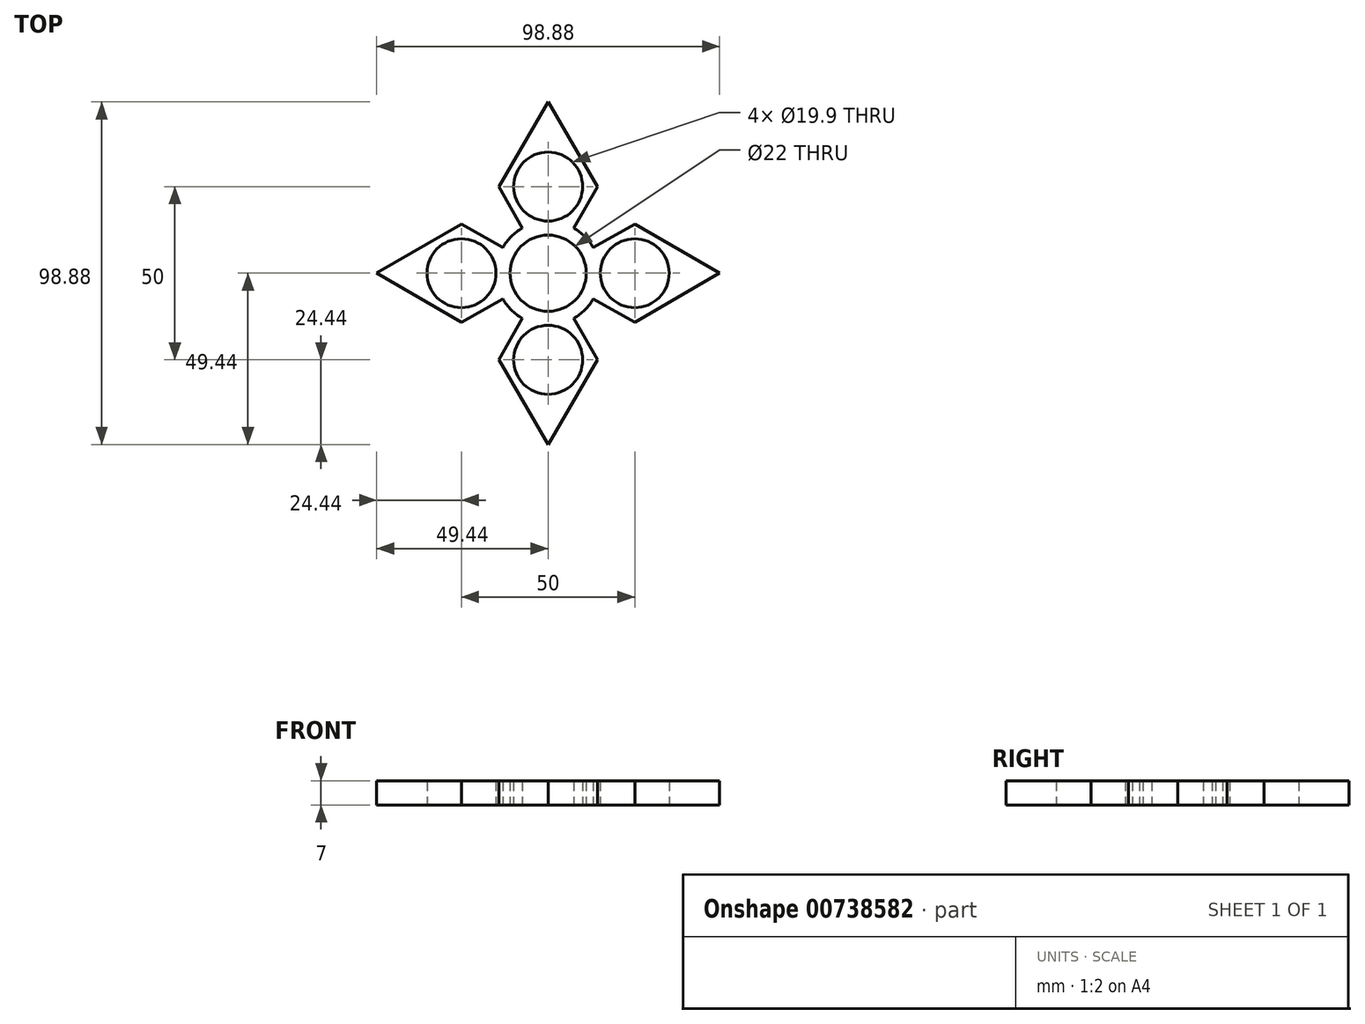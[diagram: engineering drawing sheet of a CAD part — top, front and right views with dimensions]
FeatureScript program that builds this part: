
annotation { "Feature Type Name" : "Feature", "Feature Type Description" : "" }
export const myFeature = defineFeature(function(context is Context, id is Id, definition is map)
    precondition{}
    {
        {
            var Q0;
            Q0=qCreatedBy(makeId("Top.planeOp"),FACE);
            var sketch = newSketch(context, id + "F0", { "sketchPlane" : qUnion([Q0])});
            skCircle(sketch, "E0", {"center": v(0, 0) * mm, "radius": 11 * mm});
            skArc(sketch, "E1", {"start": v(-7.41, 13.04) * mm, "mid": v(-10.6, 10.6) * mm, "end": v(-13.04, 7.41) * mm});
            skCircle(sketch, "E2", {"center": v(0, 25) * mm, "radius": 9.95 * mm});
            skLineSegment(sketch, "E3", {"start": v(0, 49.44) * mm, "end": v(14.2, 25) * mm});
            skLineSegment(sketch, "E4", {"start": v(14.2, 25) * mm, "end": v(7.41, 13.04) * mm});
            skLineSegment(sketch, "E5.MirrorCS", {"start": v(0, 49.44) * mm, "end": v(-14.2, 25) * mm});
            skLineSegment(sketch, "E6.MirrorCS", {"start": v(-14.2, 25) * mm, "end": v(-7.41, 13.04) * mm});
            skLineSegment(sketch, "E7.MirrorCS", {"start": v(14.2, -25) * mm, "end": v(7.41, -13.04) * mm});
            skLineSegment(sketch, "E8.MirrorCS", {"start": v(-14.2, -25) * mm, "end": v(-7.41, -13.04) * mm});
            skCircle(sketch, "E9.MirrorC", {"center": v(0, -25) * mm, "radius": 9.95 * mm});
            skLineSegment(sketch, "E10.MirrorCS", {"start": v(0, -49.44) * mm, "end": v(-14.2, -25) * mm});
            skLineSegment(sketch, "E11.MirrorCS", {"start": v(0, -49.44) * mm, "end": v(14.2, -25) * mm});
            skLineSegment(sketch, "E12.MirrorCS", {"start": v(25, 14.2) * mm, "end": v(13.04, 7.41) * mm});
            skLineSegment(sketch, "E13.MirrorCS", {"start": v(49.44, 0) * mm, "end": v(25, 14.2) * mm});
            skCircle(sketch, "E14.MirrorC", {"center": v(25, 0) * mm, "radius": 9.95 * mm});
            skLineSegment(sketch, "E15.MirrorCS", {"start": v(49.44, 0) * mm, "end": v(25, -14.2) * mm});
            skLineSegment(sketch, "E16.MirrorCS", {"start": v(25, -14.2) * mm, "end": v(13.04, -7.41) * mm});
            skLineSegment(sketch, "E17.MirrorCS", {"start": v(-25, 14.2) * mm, "end": v(-13.04, 7.41) * mm});
            skLineSegment(sketch, "E18.MirrorCS", {"start": v(-49.44, 0) * mm, "end": v(-25, 14.2) * mm});
            skCircle(sketch, "E19.MirrorC", {"center": v(-25, 0) * mm, "radius": 9.95 * mm});
            skLineSegment(sketch, "E20.MirrorCS", {"start": v(-49.44, 0) * mm, "end": v(-25, -14.2) * mm});
            skLineSegment(sketch, "E21.MirrorCS", {"start": v(-25, -14.2) * mm, "end": v(-13.04, -7.41) * mm});
            skArc(sketch, "E22.trimOffspring", {"start": v(13.04, 7.41) * mm, "mid": v(10.6, 10.6) * mm, "end": v(7.41, 13.04) * mm});
            skArc(sketch, "E23.trimOffspring", {"start": v(-13.04, -7.41) * mm, "mid": v(-10.6, -10.6) * mm, "end": v(-7.41, -13.04) * mm});
            skArc(sketch, "E24.trimOffspring", {"start": v(7.41, -13.04) * mm, "mid": v(10.6, -10.6) * mm, "end": v(13.04, -7.41) * mm});
            skSolve(sketch);
        }
        {
            var Q0;
            Q0 = qSketchRegion(id + "F0", true);
            extrude(context, id + "F1", {"entities" : qUnion([Q0]), "depth" : 7 * mm, "offsetDistance" : 25 * mm});
        }
    });
